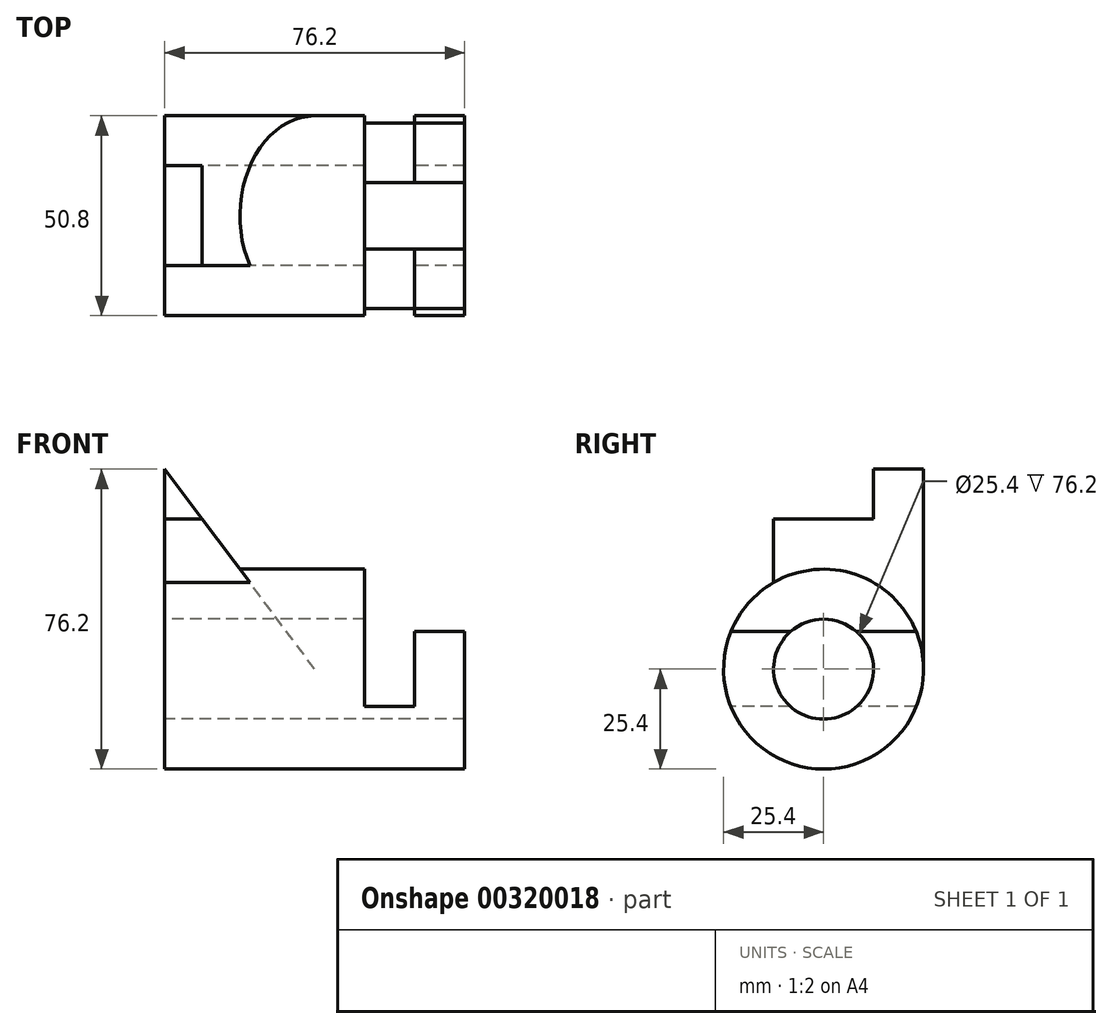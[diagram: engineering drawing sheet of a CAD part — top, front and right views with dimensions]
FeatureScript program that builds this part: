
annotation { "Feature Type Name" : "Feature", "Feature Type Description" : "" }
export const myFeature = defineFeature(function(context is Context, id is Id, definition is map)
    precondition{}
    {
        {
            var Q0;
            Q0=qCreatedBy(makeId("Right.planeOp"),FACE);
            var sketch = newSketch(context, id + "F0", { "sketchPlane" : qUnion([Q0])});
            skCircle(sketch, "E0", {"center": v(0, 0) * mm, "radius": 25.4 * mm});
            skLineSegment(sketch, "E1", {"start": v(23.55, 9.53) * mm, "end": v(8.4, 9.53) * mm});
            skCircle(sketch, "E2", {"center": v(0, 0) * mm, "radius": 12.7 * mm});
            skLineSegment(sketch, "E3.trimOffspring", {"start": v(-8.4, 9.53) * mm, "end": v(-23.55, 9.52) * mm});
            skSolve(sketch);
        }
        {
            var Q0;
            {var subQ0=sQuery(id+"F0.wireOp",EDGE,"E1");Q0=makeQuery(id+"F0.imprint","IMPRINT",FACE,{"disambiguationData":[TD([[makeQuery(id+"F0.imprint","IMPRINT",EDGE,{"derivedFrom":subQ0}),1.0]])]});}
            extrude(context, id + "F1", {"entities" : qUnion([Q0]), "depth" : 12.7 * mm});
        }
        {
            var Q0;
            Q0=makeQuery(id+"F1.opExtrude","CAP_FACE",FACE,{"disambiguationData":[OSD([sQuery(id+"F0.wireOp",EDGE,"E0"),sQuery(id+"F0.wireOp",EDGE,"E1"),sQuery(id+"F0.wireOp",EDGE,"E2"),sQuery(id+"F0.wireOp",EDGE,"E3.trimOffspring")])],"isStart":true});
            var sketch = newSketch(context, id + "F2", { "sketchPlane" : qUnion([Q0])});
            skLineSegment(sketch, "E4", {"start": v(-23.55, -9.53) * mm, "end": v(-8.4, -9.53) * mm});
            skLineSegment(sketch, "E5.0.0", {"start": v(-8.4, 9.53) * mm, "end": v(-23.55, 9.53) * mm});
            skArc(sketch, "E5.0.1", {"start": v(-23.55, 9.52) * mm, "mid": v(0, -25.4) * mm, "end": v(23.55, 9.52) * mm});
            skLineSegment(sketch, "E5.0.2", {"start": v(23.55, 9.52) * mm, "end": v(8.4, 9.53) * mm});
            skArc(sketch, "E5.0.3", {"start": v(8.4, 9.53) * mm, "mid": v(0, -12.7) * mm, "end": v(-8.4, 9.53) * mm});
            skLineSegment(sketch, "E6.trimOffspring", {"start": v(8.4, -9.53) * mm, "end": v(23.55, -9.53) * mm});
            skSolve(sketch);
        }
        {
            var Q0;
            {var subQ0=sQuery(id+"F2.wireOp",EDGE,"E4");Q0=makeQuery(id+"F2.imprint","IMPRINT",FACE,{"disambiguationData":[TD([[makeQuery(id+"F2.imprint","IMPRINT",EDGE,{"derivedFrom":subQ0}),-1.0]])]});}
            extrude(context, id + "F3", {"entities" : qUnion([Q0]), "operationType" : NewBodyOperationType.ADD, "depth" : 12.7 * mm});
        }
        {
            var Q0;
            Q0=makeQuery(id+"F3.opExtrude","CAP_EDGE",EDGE,{"disambiguationData":[OSD([sQuery(id+"F2.wireOp",EDGE,"E5.0.3")])],"isStart":false});
            cPoint(context, id + "F4", {"entities" : qUnion([Q0]), "parameter" : 0.5});
        }
        {
            var Q0;
            Q0=qCreatedBy(makeId("Right.planeOp"),FACE);
            var Q1;
            Q1 = qCreatedBy(id + "F4" ,VERTEX);
            cPlane(context, id + "F5", {"entities" : qUnion([Q0, Q1]), "cplaneType" : CPlaneType.PLANE_POINT, "offset" : 25.4 * mm, "width" : 152.4 * mm, "height" : 152.4 * mm});
        }
        {
            var Q0;
            Q0=qCreatedBy(id+"F5.planeOp",FACE);
            var sketch = newSketch(context, id + "F6", { "sketchPlane" : qUnion([Q0])});
            skCircle(sketch, "E7", {"center": v(0, 0) * mm, "radius": 25.4 * mm});
            skCircle(sketch, "E8", {"center": v(0, 0) * mm, "radius": 12.7 * mm});
            skSolve(sketch);
        }
        {
            var Q0;
            Q0=makeQuery(id+"F6.imprint","IMPRINT",FACE,{"disambiguationData":[TD([[makeQuery(id+"F6.imprint","IMPRINT",EDGE,{"derivedFrom":sQuery(id+"F6.wireOp",EDGE,"E7")}),1.0]])]});
            extrude(context, id + "F7", {"entities" : qUnion([Q0]), "operationType" : NewBodyOperationType.ADD, "oppositeDirection" : true, "depth" : 50.8 * mm});
        }
        {
            var Q0;
            Q0=makeQuery(id+"F7.opExtrude","CAP_FACE",FACE,{"disambiguationData":[OSD([sQuery(id+"F6.wireOp",EDGE,"E7"),sQuery(id+"F6.wireOp",EDGE,"E8")])],"isStart":false});
            var sketch = newSketch(context, id + "F8", { "sketchPlane" : qUnion([Q0])});
            skCircle(sketch, "E9.0.0", {"center": v(0, 0) * mm, "radius": 25.4 * mm});
            skLineSegment(sketch, "E10", {"start": v(-25.4, 0) * mm, "end": v(-25.4, 50.8) * mm});
            skLineSegment(sketch, "E11", {"start": v(-25.4, 50.8) * mm, "end": v(-12.7, 50.8) * mm});
            skLineSegment(sketch, "E12", {"start": v(-12.7, 50.8) * mm, "end": v(-12.7, 38.1) * mm});
            skLineSegment(sketch, "E13", {"start": v(-12.7, 38.1) * mm, "end": v(12.7, 38.1) * mm});
            skLineSegment(sketch, "E14", {"start": v(12.7, 38.1) * mm, "end": v(12.7, 22) * mm});
            skSolve(sketch);
        }
        {
            var Q0;
            {var subQ0=sQuery(id+"F8.wireOp",EDGE,"E10");Q0=makeQuery(id+"F8.imprint","IMPRINT",FACE,{"disambiguationData":[TD([[makeQuery(id+"F8.imprint","IMPRINT",EDGE,{"derivedFrom":subQ0}),-1.0]])]});}
            extrude(context, id + "F9", {"entities" : qUnion([Q0]), "operationType" : NewBodyOperationType.ADD, "oppositeDirection" : true, "depth" : 38.1 * mm});
        }
        {
            var Q0;
            Q0=makeQuery(id+"F9.opExtrude","SWEPT_FACE",FACE,{"disambiguationData":[OSD([sQuery(id+"F8.wireOp",EDGE,"E14")])]});
            var sketch = newSketch(context, id + "F10", { "sketchPlane" : qUnion([Q0])});
            skLineSegment(sketch, "E15", {"start": v(12.7, -25.4) * mm, "end": v(-63.5, -25.4) * mm});
            skLineSegment(sketch, "E16", {"start": v(-25.4, 25.4) * mm, "end": v(-12.7, 25.4) * mm});
            skLineSegment(sketch, "E17", {"start": v(-25.4, 25.4) * mm, "end": v(-63.5, 25.4) * mm});
            skLineSegment(sketch, "E18", {"start": v(-63.5, 25.4) * mm, "end": v(-63.5, 50.8) * mm});
            skLineSegment(sketch, "E19", {"start": v(-63.5, 50.8) * mm, "end": v(-25.4, 50.8) * mm});
            skLineSegment(sketch, "E20", {"start": v(-25.4, 50.8) * mm, "end": v(-25.4, 25.4) * mm});
            skLineSegment(sketch, "E21", {"start": v(-63.5, 25.4) * mm, "end": v(-63.5, 0) * mm});
            skLineSegment(sketch, "E22", {"start": v(-63.5, 0) * mm, "end": v(-25.4, 0) * mm});
            skLineSegment(sketch, "E23", {"start": v(-25.4, 0) * mm, "end": v(-25.4, 25.4) * mm});
            skLineSegment(sketch, "E24", {"start": v(-25.4, 0) * mm, "end": v(-63.5, 50.8) * mm});
            skSolve(sketch);
        }
        {
            var Q0;
            {var subQ1=sQuery(id+"F10.wireOp",EDGE,"E17");var subQ3=sQuery(id+"F10.wireOp",EDGE,"E24");var subQ4=makeQuery(id+"F10.imprint","INTERSECT",VERTEX,{"derivedFrom":[subQ1,subQ3]});Q0=makeQuery(id+"F10.imprint","IMPRINT",FACE,{"disambiguationData":[TD([[makeQuery(id+"F10.imprint","IMPRINT",EDGE,{"disambiguationData":[TD([[subQ4,1.0]])],"derivedFrom":subQ1}),-1.0]])]});}
            var Q1;
            {var subQ0=sQuery(id+"F10.wireOp",EDGE,"E19");Q1=makeQuery(id+"F10.imprint","IMPRINT",FACE,{"disambiguationData":[TD([[makeQuery(id+"F10.imprint","IMPRINT",EDGE,{"derivedFrom":subQ0}),-1.0]])]});}
            extrude(context, id + "F11", {"entities" : qUnion([Q0, Q1]), "operationType" : NewBodyOperationType.REMOVE, "endBound" : BoundingType.THROUGH_ALL, "oppositeDirection" : true, "depth" : 25.4 * mm});
        }
        {
            var Q0;
            {var subQ0=sQuery(id+"F8.wireOp",EDGE,"E14");var subQ1=makeQuery(id+"F9.opExtrude","CAP_FACE",FACE,{"disambiguationData":[OSD([sQuery(id+"F8.wireOp",EDGE,"E9.0.0"),sQuery(id+"F8.wireOp",EDGE,"E10"),sQuery(id+"F8.wireOp",EDGE,"E11"),sQuery(id+"F8.wireOp",EDGE,"E12"),sQuery(id+"F8.wireOp",EDGE,"E13"),subQ0])],"isStart":false});Q0=makeQuery(id+"F11.boolean.opBoolean","SPLIT",FACE,{"disambiguationData":[TD([makeQuery(id+"F9.opExtrude","SWEPT_FACE",FACE,{"disambiguationData":[OSD([subQ0])]})])],"derivedFrom":subQ1});}
            var Q1;
            {var subQ0=sQuery(id+"F8.wireOp",EDGE,"E10");var subQ1=makeQuery(id+"F9.opExtrude","CAP_FACE",FACE,{"disambiguationData":[OSD([sQuery(id+"F8.wireOp",EDGE,"E9.0.0"),subQ0,sQuery(id+"F8.wireOp",EDGE,"E11"),sQuery(id+"F8.wireOp",EDGE,"E12"),sQuery(id+"F8.wireOp",EDGE,"E13"),sQuery(id+"F8.wireOp",EDGE,"E14")])],"isStart":false});Q1=makeQuery(id+"F11.boolean.opBoolean","SPLIT",FACE,{"disambiguationData":[TD([makeQuery(id+"F9.opExtrude","SWEPT_FACE",FACE,{"disambiguationData":[OSD([subQ0])]})])],"derivedFrom":subQ1});}
            var Q2;
            Q2=makeQuery(id+"F11.boolean.opBoolean","COPY",FACE,{"derivedFrom":makeQuery(id+"F11.opExtrude","SWEPT_FACE",FACE,{"disambiguationData":[OSD([sQuery(id+"F10.wireOp",EDGE,"E24")])]})});
            extrude(context, id + "F12", {"entities" : qUnion([Q0, Q1]), "operationType" : NewBodyOperationType.REMOVE, "endBound" : BoundingType.UP_TO_SURFACE, "oppositeDirection" : true, "endBoundEntityFace" : qUnion([Q2]), "depth" : 25.4 * mm});
        }
    });
